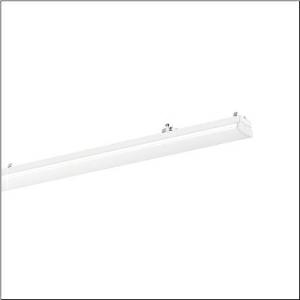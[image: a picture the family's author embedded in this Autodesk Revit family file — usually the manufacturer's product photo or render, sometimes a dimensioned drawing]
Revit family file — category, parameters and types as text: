
# Revit family: licross_11_recessed_opal_mo_51te1d7n46xg
name_source: partatom
category: Lighting Fixtures
units: mm (PartAtom-declared; Revit-internal decimal feet)

## family parameters
Cut with Voids When Loaded = No
Host = Face
Light Source = No
Part Type = Normal
Room Calculation Point = No
Round Connector Dimension = Use Diameter
Shared = No

## types (1)
- Licross 11 recessed opal MO (1 x LED, 6300 lm, 35.1 W, 4000K)
    Apparent Load = 35 VA
    CIE Flux Codes = 44 73 91 87 100
    Color Rendering = 80
    Color Temperature = 4000K
    Default Elevation = 1800 mm
    Description = Licross 11 recessed opal MO, luminaire insert, of sheet steel, coil coated, white, length: 1.500mm, width: 76mm, height: 87mm, LED rated luminous flux: 6.300lm, light colour: 840, SDCM (Standard Deviation of Colour Matching)MacAdam ≤ 2 SDCM (initial), control gear: ON/OFF, with plug, 3-pole, with phase selection, mains connection: 220..240V, AC, 50/60Hz, rated input power: 35W, internal wiring halogen-free, primary optical cover: cover, of PMMA, light emission: direct with ceiling illumination distribution, primary light characteristic: symmetric, protection rating (complete): IP54, insulation class (complete): insulation class I (protective earthing), certification: CE, ENEC, VDE, UKCA, protection symbol: D if used in an environment with non-conductive dust loads with corresponding accessories, impact resistance: IK06, permissible ambient temperature for indoor applications: -35..+45°C, corresponds to IFS (International Featured Standards) requirements for safety and quality in the food industry, reducing of maximum allowable ambient temperature of 5°C with ceiling mounting, The light source and the operating device comply with the requirements of the Ecodesign Regulation (EU) 2019/2020 and are replaceable in accordance with this regulation, packaging unit: 1 piece
    Height = 83 mm
    Lamp = 1 x LED
    Lamp Light Flux = 6300 lm
    Lamp Power = 35.1 W
    Lamp count = 1
    Length = 1500 mm
    Luminous efficacy = 179 lm/W
    Manufacturer = Siteco
    ModVariant = No
    Model = 51TE1D7N46XG
    Mounting Place = Ceiling
    Mounting Type = Pendant
    Number of Poles = 1
    OnlyDefault = Yes
    Power Factor = 1
    Product Name = Licross 11 recessed opal MO
    Product group = luminaire insert | ceiling pendant
    ProductGroupID = 901
    Protection Class = Protection class I
    Protection Degree = IP 54
    RLX_Detail_Level = 1
    RLX_Emergency_Light_Flux = 0 lm
    RLX_Emergency_Type = 0
    RLX_Emergency_Type_DB = No
    RlxData = <blob elided: 23505 chars, md5=41ac5ae8>
    Socket = socket
    Standby Power = 0 W
    System Light Flux = 6300 lm
    System Power = 35 W
    Type Comments = Product without accessories
    Type Image = l_1313666.jpg
    URL = http://relux.com
    VarID = ---
    Voltage = 0 V
    Weight = 0.00 kg
    Width = 76 mm

## geometry (parser evidence)
native form markers: Blend x4, Sweep x13
no freeform markers — native parametric forms only
